# Revit family: BE_24803_de_DE
name_source: partatom
category: Leuchten
revit_build: Autodesk Revit 2015 (Build: 20150704_0715(x64)
units: mm (PartAtom-declared; Revit-internal decimal feet)

## types (4) — shared parameters
Aktualisierung = 2016-06-09T04:10:41
Anschlussleitung = 0.5 m A05VV-F 2 x 0,75²
BEGA_Dummy = Nein
BEGA_IES = Ja
BEGA_Intern = Ja
BEGA_Intern_Konstruktion = Ja
BEGA_Intern_an = Ja
BEGA_Intern_aus = Ja
Befestigungsabstand = 50 mm
Beschreibung = Deckeneinbau-Tiefstrahler
Beschreibung_Sonderanfertigung = Hier können Sie Informationen zur Sonderanfertigung eintragen.
Bestellnummer_Einbaugehäuse = ---
Bestellnummer_Netzteil_DALI_steuerbar = ---
Bestellnummer_Netzteil_dimmbar_1_bis_10V = ---
CE_Konformität = ja
Einbau_in_Wärmedämmung = ungeeignet
Einbaugehäuse = Nein
Einbautiefe = 70 mm
Einbauöffnung = 177 x 177 mm
Energieeffizienzklasse = LED A++ - A
Farbfilter = 16777215
Farbtemperaturverschiebung bei Dämpfen der Lampe = <Keine Auswahl>
Farbwiedergabeindex = Ra > 80
Gewicht = 1.3 kg
Hersteller = BEGA
Lampe = LED 33.6 W
Lampenlichtstrom = 4640 lm
Lastklassifizierung = Beleuchtung
Lebensdauerkriterien = L70 = 50.000 h
Leuchtenlichtstrom = 2358 lm
Logo = BEGA_Logo.png
Material_02 = BEGA_Oberfläche_Silber_matt
Material_03 = BEGA_Oberfläche_Weiss_matt
Material_06 = BEGA_Oberfläche_Edelstahl_gebürstet
Material_10 = BEGA_Glas_matt
Neigungswinkel = 0.00°
Netzteil_DALI_steuerbar = Nein
Netzteil_dimmbar_1_bis_10V = Nein
Produktdatenblatt = http://www.bega.de
Scheinlast = 0 VA
Schutzart = IP 65
Schutzklasse = III
Sonderanfertigung = Nein
Spannung = 0 V
Strom = 0,7 A
Typenbild = 24803.png
URL = http://www.bega.de
Umgebungstemperatur = 25 °C
zero-valued in all types: Vorgabe-Ansicht

## per-type parameters (varying)
| type | Bestellnummer | Datei für fotometrisches Netz | Farbtemperatur | LED_Modulbezeichnung | M_A | M_W | Modell |
| BEGA_24803_Silber_K4 | 24803AK4 | BE_24803K4.IES | 4000 K | 4x LED-0588/840 | Ja | Nein | 24803AK4 |
| BEGA_24803_Weiß_K3 | 24803 | BE_24803.IES | 3000 K | 4x LED-0588/830 | Nein | Ja | 24803 |
| BEGA_24803_Weiß_K4 | 24803K4 | BE_24803K4.IES | 4000 K | 4x LED-0588/840 | Nein | Ja | 24803K4 |
| BEGA_24803_Silber_K3 | 24803A | BE_24803.IES | 3000 K | 4x LED-0588/830 | Ja | Nein | 24803A |
